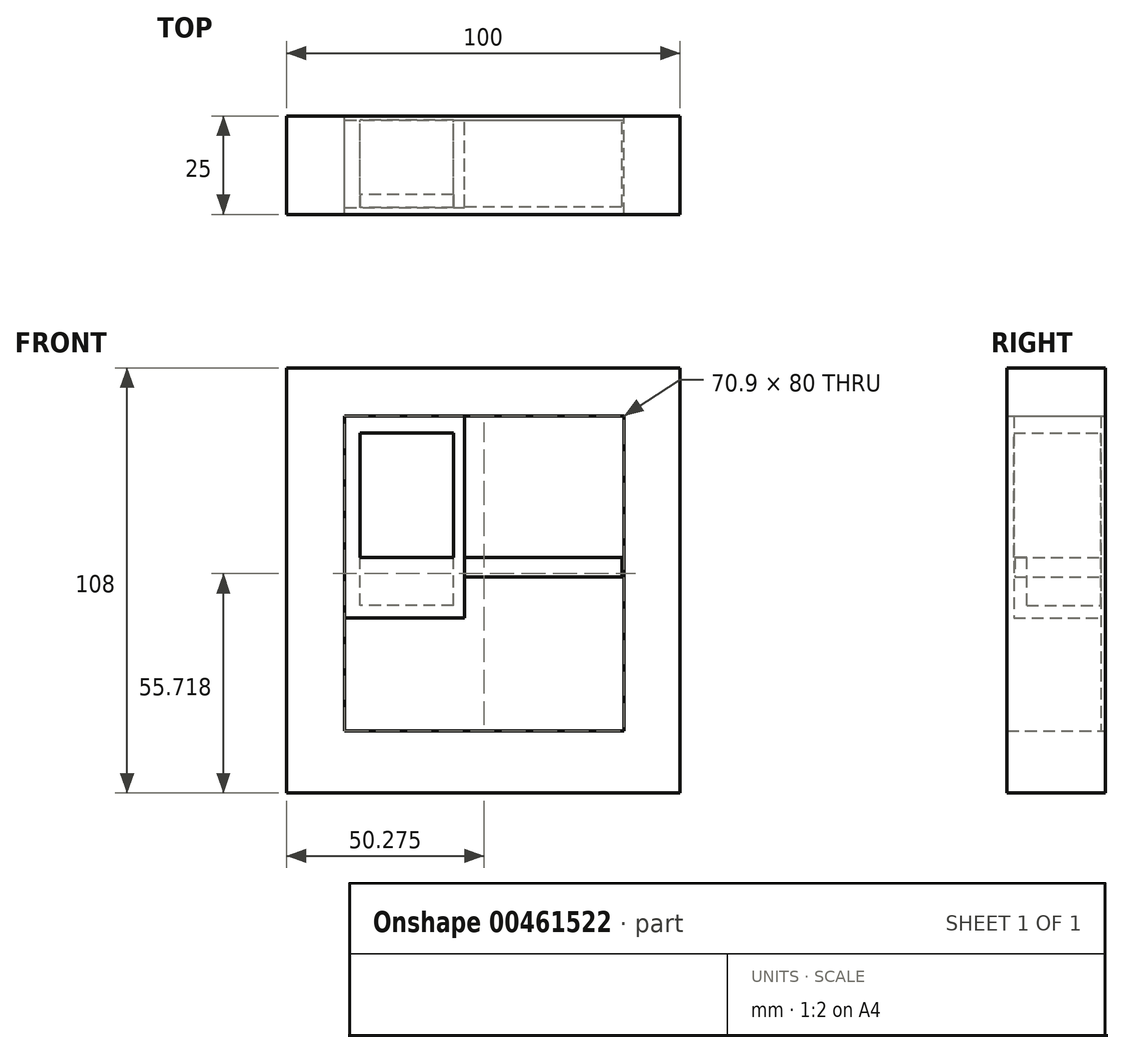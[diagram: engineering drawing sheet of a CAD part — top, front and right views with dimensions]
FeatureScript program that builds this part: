
annotation { "Feature Type Name" : "Feature", "Feature Type Description" : "" }
export const myFeature = defineFeature(function(context is Context, id is Id, definition is map)
    precondition{}
    {
        {
            var Q0;
            Q0=qCreatedBy(makeId("Front.planeOp"),FACE);
            var sketch = newSketch(context, id + "F0", { "sketchPlane" : qUnion([Q0])});
            skLineSegment(sketch, "E0.bottom", {"start": v(-45.3, 48.1) * mm, "end": v(54.7, 48.1) * mm});
            skLineSegment(sketch, "E0.top", {"start": v(-45.3, -51.9) * mm, "end": v(54.7, -51.9) * mm});
            skLineSegment(sketch, "E0.left", {"start": v(-45.3, 48.1) * mm, "end": v(-45.3, -51.9) * mm});
            skLineSegment(sketch, "E0.right", {"start": v(54.7, 48.1) * mm, "end": v(54.7, -51.9) * mm});
            skLineSegment(sketch, "E1.bottom", {"start": v(-39.57, 35.83) * mm, "end": v(40.43, 35.83) * mm});
            skLineSegment(sketch, "E1.top", {"start": v(-39.57, -44.17) * mm, "end": v(40.43, -44.17) * mm});
            skLineSegment(sketch, "E1.left", {"start": v(-39.57, 35.83) * mm, "end": v(-39.57, -44.17) * mm});
            skLineSegment(sketch, "E1.right", {"start": v(40.43, 35.83) * mm, "end": v(40.43, -44.17) * mm});
            skSolve(sketch);
        }
        {
            var Q0;
            Q0=makeQuery(id+"F0.imprint","IMPRINT",FACE,{"disambiguationData":[TD([[makeQuery(id+"F0.imprint","IMPRINT",EDGE,{"derivedFrom":sQuery(id+"F0.wireOp",EDGE,"E0.bottom")}),-1.0]])]});
            extrude(context, id + "F1", {"entities" : qUnion([Q0]), "depth" : 25 * mm});
        }
        {
            var Q0;
            Q0=makeQuery(id+"F1.opExtrude","SWEPT_FACE",FACE,{"disambiguationData":[OSD([sQuery(id+"F0.wireOp",EDGE,"E1.left")])]});
            extrude(context, id + "F2", {"entities" : qUnion([Q0]), "operationType" : NewBodyOperationType.ADD, "depth" : 9.1 * mm});
        }
        {
            var Q0;
            Q0=makeQuery(id+"F1.opExtrude","SWEPT_FACE",FACE,{"disambiguationData":[OSD([sQuery(id+"F0.wireOp",EDGE,"E0.top")])]});
            extrude(context, id + "F3", {"entities" : qUnion([Q0]), "operationType" : NewBodyOperationType.ADD, "depth" : 8 * mm});
        }
        {
            var Q0;
            {var subQ0=sQuery(id+"F0.wireOp",EDGE,"E0.top");var subQ1=sQuery(id+"F0.wireOp",EDGE,"E1.left");Q0=makeQuery(id+"F3.boolean.opBoolean","MERGE",FACE,{"derivedFrom":[makeQuery(id+"F2.boolean.opBoolean","MERGE",FACE,{"derivedFrom":[makeQuery(id+"F1.opExtrude","CAP_FACE",FACE,{"disambiguationData":[OSD([sQuery(id+"F0.wireOp",EDGE,"E0.bottom"),subQ0,sQuery(id+"F0.wireOp",EDGE,"E0.left"),sQuery(id+"F0.wireOp",EDGE,"E0.right"),sQuery(id+"F0.wireOp",EDGE,"E1.bottom"),sQuery(id+"F0.wireOp",EDGE,"E1.top"),subQ1,sQuery(id+"F0.wireOp",EDGE,"E1.right")])],"isStart":true}),makeQuery(id+"F2.opExtrude","SWEPT_FACE",FACE,{"disambiguationData":[OSD([subQ1]),TDD([makeQuery(id+"F1.opExtrude","CAP_EDGE",EDGE,{"disambiguationData":[OSD([subQ1])],"isStart":true})])]})]}),makeQuery(id+"F3.opExtrude","SWEPT_FACE",FACE,{"disambiguationData":[OSD([subQ0]),TDD([makeQuery(id+"F1.opExtrude","CAP_EDGE",EDGE,{"disambiguationData":[OSD([subQ0])],"isStart":true})])]})]});}
            var sketch = newSketch(context, id + "F4", { "sketchPlane" : qUnion([Q0])});
            skLineSegment(sketch, "E2.bottom", {"start": v(-40.43, 35.83) * mm, "end": v(30.47, 35.83) * mm});
            skLineSegment(sketch, "E2.top", {"start": v(-40.43, -44.17) * mm, "end": v(30.47, -44.17) * mm});
            skLineSegment(sketch, "E2.left", {"start": v(-40.43, 35.83) * mm, "end": v(-40.43, -44.17) * mm});
            skLineSegment(sketch, "E2.right", {"start": v(30.47, 35.83) * mm, "end": v(30.47, -44.17) * mm});
            skSolve(sketch);
        }
        {
            var Q0;
            Q0=makeQuery(id+"F4.imprint","IMPRINT",FACE,{"disambiguationData":[TD([[makeQuery(id+"F4.imprint","IMPRINT",EDGE,{"derivedFrom":sQuery(id+"F4.wireOp",EDGE,"E2.bottom")}),1.0]])]});
            extrude(context, id + "F5", {"entities" : qUnion([Q0]), "oppositeDirection" : true, "depth" : 1.1 * mm});
        }
        {
            var Q0;
            Q0=makeQuery(id+"F5.opExtrude","CAP_FACE",FACE,{"disambiguationData":[OSD([sQuery(id+"F4.wireOp",EDGE,"E2.bottom"),sQuery(id+"F4.wireOp",EDGE,"E2.top"),sQuery(id+"F4.wireOp",EDGE,"E2.left"),sQuery(id+"F4.wireOp",EDGE,"E2.right")])],"isStart":false});
            var sketch = newSketch(context, id + "F6", { "sketchPlane" : qUnion([Q0])});
            skLineSegment(sketch, "E3", {"start": v(0, 35.83) * mm, "end": v(0, -15.42) * mm});
            skLineSegment(sketch, "E4", {"start": v(0, -15.42) * mm, "end": v(-30.47, -15.42) * mm});
            skPoint(sketch, "E4.endSnap0", {"position": v(-30.47, -4.17) * mm});
            skLineSegment(sketch, "E5", {"start": v(-30.47, -15.42) * mm, "end": v(-30.47, 35.83) * mm});
            skLineSegment(sketch, "E6", {"start": v(-30.47, 35.83) * mm, "end": v(0, 35.83) * mm});
            skSolve(sketch);
        }
        {
            var Q0;
            Q0=makeQuery(id+"F6.imprint","IMPRINT",FACE,{"disambiguationData":[TD([[makeQuery(id+"F6.imprint","IMPRINT",EDGE,{"derivedFrom":sQuery(id+"F6.wireOp",EDGE,"E3")}),-1.0]])]});
            var sketch = newSketch(context, id + "F7", { "sketchPlane" : qUnion([Q0])});
            skLineSegment(sketch, "E7.bottom", {"start": v(-2.89, -12.23) * mm, "end": v(-26.63, -12.23) * mm});
            skLineSegment(sketch, "E7.top", {"start": v(-2.89, 31.54) * mm, "end": v(-26.63, 31.54) * mm});
            skLineSegment(sketch, "E7.left", {"start": v(-2.89, -12.23) * mm, "end": v(-2.89, 31.54) * mm});
            skLineSegment(sketch, "E7.right", {"start": v(-26.63, -12.23) * mm, "end": v(-26.63, 31.54) * mm});
            skSolve(sketch);
        }
        {
            var Q0;
            Q0=makeQuery(id+"F7.imprint","IMPRINT",FACE,{"disambiguationData":[TD([[makeQuery(id+"F7.imprint","IMPRINT",EDGE,{"derivedFrom":sQuery(id+"F7.wireOp",EDGE,"E7.bottom")}),1.0]])]});
            extrude(context, id + "F8", {"entities" : qUnion([Q0]), "depth" : 22.2 * mm});
        }
        {
            var Q0;
            {var subQ2=sQuery(id+"F6.wireOp",EDGE,"E3");Q0=makeQuery(id+"F6.imprint","IMPRINT",FACE,{"disambiguationData":[TD([[makeQuery(id+"F6.imprint","IMPRINT",EDGE,{"derivedFrom":subQ2}),1.0]])]});}
            var sketch = newSketch(context, id + "F9", { "sketchPlane" : qUnion([Q0])});
            skLineSegment(sketch, "E8", {"start": v(0, 0) * mm, "end": v(40, 0) * mm});
            skLineSegment(sketch, "E9", {"start": v(40, 0) * mm, "end": v(40, -5) * mm});
            skLineSegment(sketch, "E10", {"start": v(40, -5) * mm, "end": v(0, -5) * mm});
            skLineSegment(sketch, "E11", {"start": v(0, -5) * mm, "end": v(0, 0) * mm});
            skSolve(sketch);
        }
        {
            var Q0;
            Q0=makeQuery(id+"F9.imprint","IMPRINT",FACE,{"disambiguationData":[TD([[makeQuery(id+"F9.imprint","IMPRINT",EDGE,{"derivedFrom":sQuery(id+"F9.wireOp",EDGE,"E8")}),-1.0]])]});
            extrude(context, id + "F10", {"entities" : qUnion([Q0]), "depth" : 21.9 * mm});
        }
        {
            var Q0;
            Q0=makeQuery(id+"F8.opExtrude","CAP_FACE",FACE,{"disambiguationData":[OSD([sQuery(id+"F6.wireOp",EDGE,"E3"),sQuery(id+"F6.wireOp",EDGE,"E4"),sQuery(id+"F6.wireOp",EDGE,"E5"),sQuery(id+"F6.wireOp",EDGE,"E6"),sQuery(id+"F7.wireOp",EDGE,"E7.bottom"),sQuery(id+"F7.wireOp",EDGE,"E7.top"),sQuery(id+"F7.wireOp",EDGE,"E7.left"),sQuery(id+"F7.wireOp",EDGE,"E7.right")])],"isStart":false});
            var sketch = newSketch(context, id + "F11", { "sketchPlane" : qUnion([Q0])});
            skLineSegment(sketch, "E12.bottom", {"start": v(-26.63, -12.23) * mm, "end": v(-2.89, -12.23) * mm});
            skLineSegment(sketch, "E12.top", {"start": v(-26.63, 0) * mm, "end": v(-2.89, 0) * mm});
            skLineSegment(sketch, "E12.left", {"start": v(-26.63, -12.23) * mm, "end": v(-26.63, 0) * mm});
            skLineSegment(sketch, "E12.right", {"start": v(-2.89, -12.23) * mm, "end": v(-2.89, 0) * mm});
            skSolve(sketch);
        }
        {
            var Q0;
            Q0=makeQuery(id+"F11.imprint","IMPRINT",FACE,{"disambiguationData":[TD([[makeQuery(id+"F11.imprint","IMPRINT",EDGE,{"derivedFrom":sQuery(id+"F11.wireOp",EDGE,"E12.bottom")}),-1.0]])]});
            extrude(context, id + "F12", {"entities" : qUnion([Q0]), "operationType" : NewBodyOperationType.ADD, "oppositeDirection" : true, "depth" : 3.3 * mm});
        }
        {
            var Q0;
            Q0=makeQuery(id+"F12.boolean.opBoolean","MERGE",FACE,{"derivedFrom":[makeQuery(id+"F8.opExtrude","CAP_FACE",FACE,{"disambiguationData":[OSD([sQuery(id+"F6.wireOp",EDGE,"E3"),sQuery(id+"F6.wireOp",EDGE,"E4"),sQuery(id+"F6.wireOp",EDGE,"E5"),sQuery(id+"F6.wireOp",EDGE,"E6"),sQuery(id+"F7.wireOp",EDGE,"E7.bottom"),sQuery(id+"F7.wireOp",EDGE,"E7.top"),sQuery(id+"F7.wireOp",EDGE,"E7.left"),sQuery(id+"F7.wireOp",EDGE,"E7.right")])],"isStart":false}),makeQuery(id+"F12.opExtrude","CAP_FACE",FACE,{"disambiguationData":[OSD([sQuery(id+"F11.wireOp",EDGE,"E12.bottom"),sQuery(id+"F11.wireOp",EDGE,"E12.top"),sQuery(id+"F11.wireOp",EDGE,"E12.left"),sQuery(id+"F11.wireOp",EDGE,"E12.right")])],"isStart":true})]});
            var sketch = newSketch(context, id + "F13", { "sketchPlane" : qUnion([Q0])});
            skSolve(sketch);
        }
        {
            var Q0;
            Q0=makeQuery(id+"F13.imprint","IMPRINT",FACE,{"disambiguationData":[TD([[makeQuery(id+"F13.imprint","IMPRINT",EDGE,{"derivedFrom":makeQuery(id+"F8.opExtrude","CAP_EDGE",EDGE,{"disambiguationData":[OSD([sQuery(id+"F7.wireOp",EDGE,"E7.top")])],"isStart":false})}),-1.0]])]});
            var sketch = newSketch(context, id + "F14", { "sketchPlane" : qUnion([Q0])});
            skCircle(sketch, "E13", {"center": v(-15.27, -7.71) * mm, "radius": 2.93 * mm});
            skSolve(sketch);
        }
        {
            var Q0;
            Q0=makeQuery(id+"F14.imprint","IMPRINT",FACE,{"disambiguationData":[TD([[makeQuery(id+"F14.imprint","IMPRINT",EDGE,{"derivedFrom":sQuery(id+"F14.wireOp",EDGE,"E13")}),1.0]])]});
            extrude(context, id + "F15", {"entities" : qUnion([Q0]), "operationType" : NewBodyOperationType.ADD, "oppositeDirection" : true, "depth" : 1.3 * mm});
        }
    });
